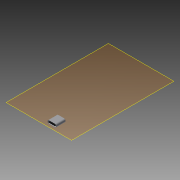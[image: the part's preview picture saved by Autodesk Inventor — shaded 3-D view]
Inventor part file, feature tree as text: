
AUTODESK INVENTOR PART (.ipt)
format: ipt  version: 2013 SP2 (Build 170200200, 200)  size: 124,928 bytes
history: native  units: mm
features: extrude x2, sketch x2, plane x1, fillet x1, shell x1
ambient origin geometry x8: Origin, YZ Plane, XZ Plane, XY Plane, X Axis, Y Axis, Z Axis, Center Point
bodies: Solid1 (feature_tree)
feature tree (7):
  plane  "Work Plane1"
  extrude  "Extrusion1"  Depth=10.0mm
  fillet  "Fillet1"  Radius=3.5mm
  shell  "Shell1"  Thickness=1.5mm
  extrude  "Extrusion2"  Depth=1.0mm
  sketch  "Sketch1"  dims[d0=9.3mm d2=10.0mm d3=3.5mm d4=0.0mm d5=1.5mm]
  sketch  "Sketch2"  dims[d6=0.2mm d7=1.0mm d9=3.5mm d10=0.0mm]
